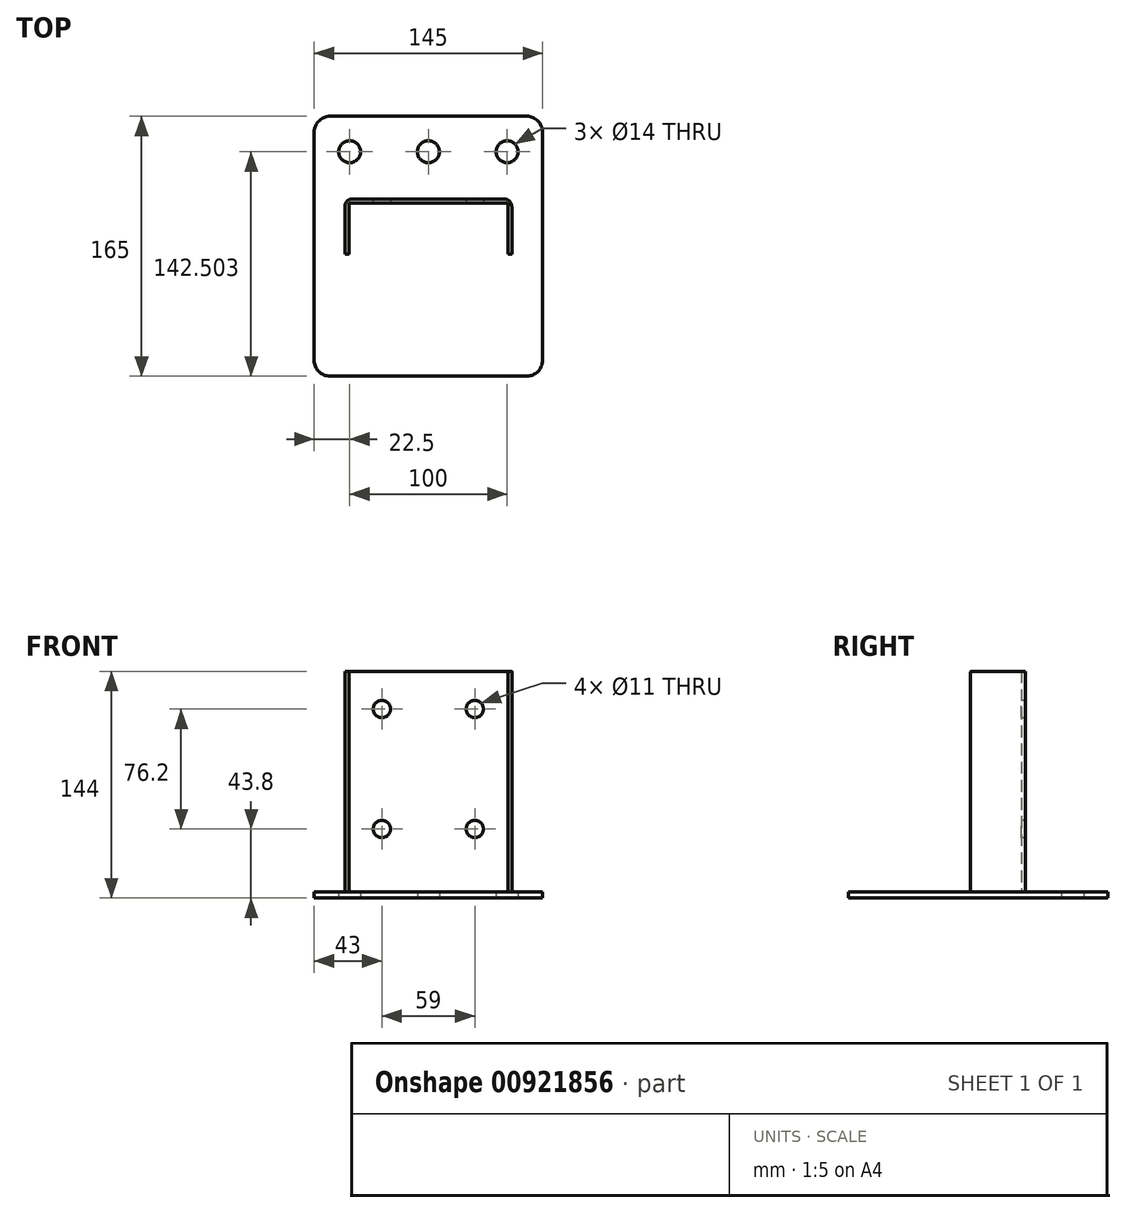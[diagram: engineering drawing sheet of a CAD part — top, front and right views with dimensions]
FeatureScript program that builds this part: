
annotation { "Feature Type Name" : "Feature", "Feature Type Description" : "" }
export const myFeature = defineFeature(function(context is Context, id is Id, definition is map)
    precondition{}
    {
        {
            var Q0;
            Q0=qCreatedBy(makeId("Top.planeOp"),FACE);
            var sketch = newSketch(context, id + "F0", { "sketchPlane" : qUnion([Q0])});
            skLineSegment(sketch, "E0.bottom", {"start": v(-145, -40.68) * mm, "end": v(0, -40.68) * mm});
            skLineSegment(sketch, "E0.top", {"start": v(-145, 124.32) * mm, "end": v(0, 124.32) * mm});
            skLineSegment(sketch, "E0.left", {"start": v(-145, -40.68) * mm, "end": v(-145, 124.32) * mm});
            skLineSegment(sketch, "E0.right", {"start": v(0, -40.68) * mm, "end": v(0, 124.32) * mm});
            skSolve(sketch);
        }
        {
            var Q0;
            Q0=makeQuery(id+"F0.imprint","IMPRINT",FACE,{"disambiguationData":[TD([[makeQuery(id+"F0.imprint","IMPRINT",EDGE,{"derivedFrom":sQuery(id+"F0.wireOp",EDGE,"E0.bottom")}),1.0]])]});
            extrude(context, id + "F1", {"entities" : qUnion([Q0]), "depth" : 4 * mm, "offsetDistance" : 25 * mm});
        }
        {
            var Q0;
            Q0=makeQuery(id+"F1.opExtrude","SWEPT_EDGE",EDGE,{"disambiguationData":[OSD([sQuery(id+"F0.wireOp",EDGE,"E0.bottom"),sQuery(id+"F0.wireOp",EDGE,"E0.right")])]});
            var Q1;
            Q1=makeQuery(id+"F1.opExtrude","SWEPT_EDGE",EDGE,{"disambiguationData":[OSD([sQuery(id+"F0.wireOp",EDGE,"E0.top"),sQuery(id+"F0.wireOp",EDGE,"E0.right")])]});
            var Q2;
            Q2=makeQuery(id+"F1.opExtrude","SWEPT_EDGE",EDGE,{"disambiguationData":[OSD([sQuery(id+"F0.wireOp",EDGE,"E0.top"),sQuery(id+"F0.wireOp",EDGE,"E0.left")])]});
            var Q3;
            Q3=makeQuery(id+"F1.opExtrude","SWEPT_EDGE",EDGE,{"disambiguationData":[OSD([sQuery(id+"F0.wireOp",EDGE,"E0.bottom"),sQuery(id+"F0.wireOp",EDGE,"E0.left")])]});
            fillet(context, id + "F2", {"entities" : qUnion([Q0, Q1, Q2, Q3]), "radius" : 10 * mm, "tangentPropagation" : true, "allowEdgeOverflow" : false});
        }
        {
            var Q0;
            Q0=makeQuery(id+"F1.opExtrude","CAP_FACE",FACE,{"disambiguationData":[OSD([sQuery(id+"F0.wireOp",EDGE,"E0.bottom"),sQuery(id+"F0.wireOp",EDGE,"E0.top"),sQuery(id+"F0.wireOp",EDGE,"E0.left"),sQuery(id+"F0.wireOp",EDGE,"E0.right")])],"isStart":false});
            var sketch = newSketch(context, id + "F3", { "sketchPlane" : qUnion([Q0])});
            skLineSegment(sketch, "E1", {"start": v(-19.5, 71.82) * mm, "end": v(-19.5, 36.82) * mm});
            skLineSegment(sketch, "E2", {"start": v(-19.5, 36.82) * mm, "end": v(-22, 36.82) * mm});
            skLineSegment(sketch, "E3", {"start": v(-22, 36.82) * mm, "end": v(-22, 69.32) * mm});
            skLineSegment(sketch, "E4", {"start": v(-22, 69.32) * mm, "end": v(-123, 69.32) * mm});
            skLineSegment(sketch, "E5", {"start": v(-123, 69.32) * mm, "end": v(-123, 36.82) * mm});
            skLineSegment(sketch, "E6", {"start": v(-123, 36.82) * mm, "end": v(-125.5, 36.82) * mm});
            skLineSegment(sketch, "E7", {"start": v(-125.5, 36.82) * mm, "end": v(-125.5, 71.82) * mm});
            skLineSegment(sketch, "E8", {"start": v(-19.5, 71.82) * mm, "end": v(-125.5, 71.82) * mm});
            skSolve(sketch);
        }
        {
            var Q0;
            Q0=makeQuery(id+"F3.imprint","IMPRINT",FACE,{"disambiguationData":[TD([[makeQuery(id+"F3.imprint","IMPRINT",EDGE,{"derivedFrom":sQuery(id+"F3.wireOp",EDGE,"E1")}),-1.0]])]});
            extrude(context, id + "F4", {"entities" : qUnion([Q0]), "operationType" : NewBodyOperationType.ADD, "depth" : 140 * mm, "offsetDistance" : 25 * mm});
        }
        {
            var Q0;
            Q0=makeQuery(id+"F4.opExtrude","SWEPT_EDGE",EDGE,{"disambiguationData":[OSD([sQuery(id+"F3.wireOp",EDGE,"E7"),sQuery(id+"F3.wireOp",EDGE,"E8")])]});
            var Q1;
            Q1=makeQuery(id+"F4.opExtrude","SWEPT_EDGE",EDGE,{"disambiguationData":[OSD([sQuery(id+"F3.wireOp",EDGE,"E1"),sQuery(id+"F3.wireOp",EDGE,"E8")])]});
            fillet(context, id + "F5", {"entities" : qUnion([Q0, Q1]), "radius" : 5 * mm, "tangentPropagation" : true, "allowEdgeOverflow" : false});
        }
        {
            var Q0;
            Q0=makeQuery(id+"F4.opExtrude","SWEPT_EDGE",EDGE,{"disambiguationData":[OSD([sQuery(id+"F3.wireOp",EDGE,"E3"),sQuery(id+"F3.wireOp",EDGE,"E4")])]});
            var Q1;
            Q1=makeQuery(id+"F4.opExtrude","SWEPT_EDGE",EDGE,{"disambiguationData":[OSD([sQuery(id+"F3.wireOp",EDGE,"E4"),sQuery(id+"F3.wireOp",EDGE,"E5")])]});
            fillet(context, id + "F6", {"entities" : qUnion([Q0, Q1]), "radius" : 1 * mm, "tangentPropagation" : true, "allowEdgeOverflow" : false});
        }
        {
            var Q0;
            Q0=makeQuery(id+"F4.opExtrude","CAP_EDGE",EDGE,{"disambiguationData":[OSD([sQuery(id+"F3.wireOp",EDGE,"E6")])],"isStart":false});
            var Q1;
            Q1=makeQuery(id+"F4.opExtrude","CAP_EDGE",EDGE,{"disambiguationData":[OSD([sQuery(id+"F3.wireOp",EDGE,"E2")])],"isStart":false});
            fillet(context, id + "F7", {"entities" : qUnion([Q0, Q1]), "radius" : 1 * mm, "tangentPropagation" : true, "allowEdgeOverflow" : false});
        }
        {
            var Q0;
            Q0=makeQuery(id+"F1.opExtrude","CAP_FACE",FACE,{"disambiguationData":[OSD([sQuery(id+"F0.wireOp",EDGE,"E0.bottom"),sQuery(id+"F0.wireOp",EDGE,"E0.top"),sQuery(id+"F0.wireOp",EDGE,"E0.left"),sQuery(id+"F0.wireOp",EDGE,"E0.right")])],"isStart":false});
            var sketch = newSketch(context, id + "F8", { "sketchPlane" : qUnion([Q0])});
            skCircle(sketch, "E9", {"center": v(-22.5, 101.82) * mm, "radius": 7.47 * mm});
            skCircle(sketch, "E10", {"center": v(-72.5, 101.82) * mm, "radius": 7.47 * mm});
            skCircle(sketch, "E11", {"center": v(-122.5, 101.82) * mm, "radius": 7.47 * mm});
            skSolve(sketch);
        }
        {
            var Q0;
            Q0=sQuery(id+"F8.wireOp",VERTEX,"E9.center");
            var Q1;
            Q1=sQuery(id+"F8.wireOp",VERTEX,"E10.center");
            var Q2;
            Q2=sQuery(id+"F8.wireOp",VERTEX,"E11.center");
            var Q3;
            Q3=makeQuery(id+"F1.opExtrude","SWEPT_BODY",BODY,{"disambiguationData":[OSD([sQuery(id+"F0.wireOp",EDGE,"E0.bottom"),sQuery(id+"F0.wireOp",EDGE,"E0.top"),sQuery(id+"F0.wireOp",EDGE,"E0.left"),sQuery(id+"F0.wireOp",EDGE,"E0.right")])]});
            hole(context, id + "F9", {"style" : HoleStyle.SIMPLE, "endStyle" : HoleEndStyle.THROUGH, "holeDiameter" : 14 * mm, "majorDiameter" : 5 * mm, "isTappedThrough" : true, "tappedDepth" : 12 * mm, "tapClearance" : 3, "locations" : qUnion([Q0, Q1, Q2]), "scope" : qUnion([Q3]), "startStyle" : HoleStartStyle.PART});
        }
        {
            var Q0;
            Q0=makeQuery(id+"F4.opExtrude","SWEPT_FACE",FACE,{"disambiguationData":[OSD([sQuery(id+"F3.wireOp",EDGE,"E8")])]});
            var sketch = newSketch(context, id + "F10", { "sketchPlane" : qUnion([Q0])});
            skCircle(sketch, "E12", {"center": v(43, 120) * mm, "radius": 5.5 * mm});
            skCircle(sketch, "E13.0.1.0", {"center": v(43, 43.8) * mm, "radius": 5.5 * mm});
            skCircle(sketch, "E13.1.0.0", {"center": v(102, 120) * mm, "radius": 5.5 * mm});
            skCircle(sketch, "E13.1.1.0", {"center": v(102, 43.8) * mm, "radius": 5.5 * mm});
            skLineSegment(sketch, "E13.direction1", {"start": v(43, 120) * mm, "end": v(102, 120) * mm, "construction": true});
            skLineSegment(sketch, "E13.direction2", {"start": v(43, 120) * mm, "end": v(43, 43.8) * mm, "construction": true});
            skSolve(sketch);
        }
        {
            var Q0;
            Q0=sQuery(id+"F10.wireOp",VERTEX,"E13.direction1.end");
            var Q1;
            Q1=sQuery(id+"F10.wireOp",VERTEX,"E13.direction1.start");
            var Q2;
            Q2=sQuery(id+"F10.wireOp",VERTEX,"E13.direction2.end");
            var Q3;
            Q3=sQuery(id+"F10.wireOp",VERTEX,"E13.1.1.0.center");
            var Q4;
            Q4=makeQuery(id+"F1.opExtrude","SWEPT_BODY",BODY,{"disambiguationData":[OSD([sQuery(id+"F0.wireOp",EDGE,"E0.bottom"),sQuery(id+"F0.wireOp",EDGE,"E0.top"),sQuery(id+"F0.wireOp",EDGE,"E0.left"),sQuery(id+"F0.wireOp",EDGE,"E0.right")])]});
            hole(context, id + "F11", {"style" : HoleStyle.SIMPLE, "endStyle" : HoleEndStyle.THROUGH, "holeDiameter" : 11 * mm, "majorDiameter" : 5 * mm, "isTappedThrough" : true, "tappedDepth" : 12 * mm, "tapClearance" : 3, "locations" : qUnion([Q0, Q1, Q2, Q3]), "scope" : qUnion([Q4]), "startStyle" : HoleStartStyle.PART});
        }
    });
